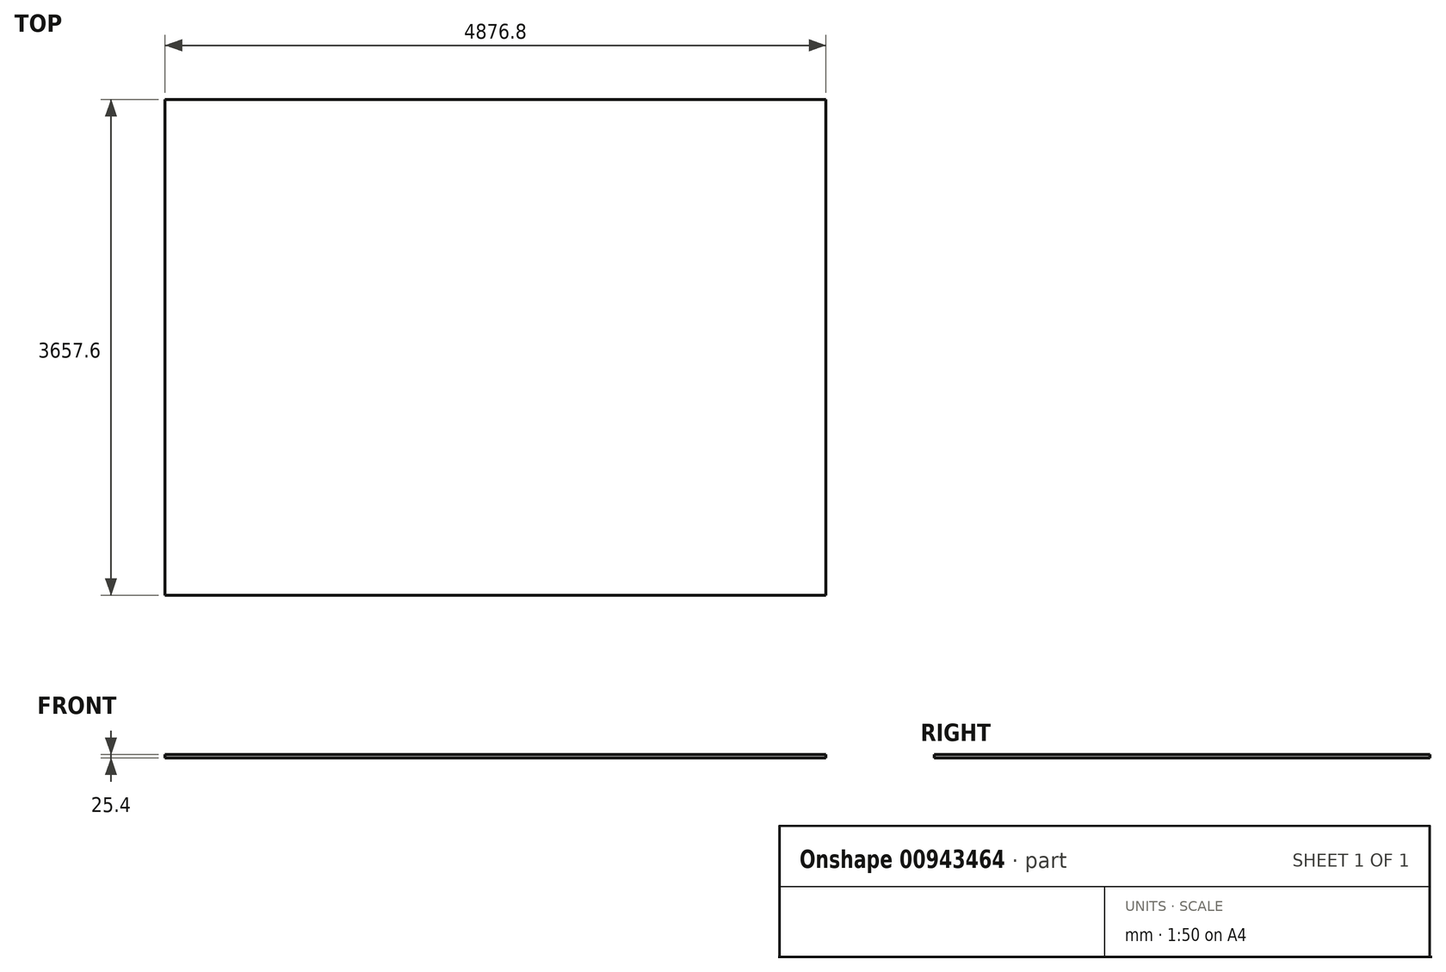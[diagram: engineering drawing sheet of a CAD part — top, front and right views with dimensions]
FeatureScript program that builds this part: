
annotation { "Feature Type Name" : "Feature", "Feature Type Description" : "" }
export const myFeature = defineFeature(function(context is Context, id is Id, definition is map)
    precondition{}
    {
        {
            var Q0;
            Q0=qCreatedBy(makeId("Top.planeOp"),FACE);
            var sketch = newSketch(context, id + "F0", { "sketchPlane" : qUnion([Q0])});
            skLineSegment(sketch, "E0.bottom", {"start": v(-2410.92, -1828.8) * mm, "end": v(2465.88, -1828.8) * mm});
            skLineSegment(sketch, "E0.top", {"start": v(-2410.92, 1828.8) * mm, "end": v(2465.88, 1828.8) * mm});
            skLineSegment(sketch, "E0.left", {"start": v(-2410.92, -1828.8) * mm, "end": v(-2410.92, 1828.8) * mm});
            skLineSegment(sketch, "E0.right", {"start": v(2465.88, -1828.8) * mm, "end": v(2465.88, 1828.8) * mm});
            skPoint(sketch, "E0.middle", {"position": v(27.48, 0) * mm});
            skSolve(sketch);
        }
        {
            var Q0;
            Q0=makeQuery(id+"F0.imprint","IMPRINT",FACE,{"disambiguationData":[TD([[makeQuery(id+"F0.imprint","IMPRINT",EDGE,{"derivedFrom":sQuery(id+"F0.wireOp",EDGE,"E0.bottom")}),1.0]])]});
            extrude(context, id + "F1", {"entities" : qUnion([Q0]), "oppositeDirection" : true, "depth" : 25.4 * mm, "offsetDistance" : 25.4 * mm});
        }
    });
